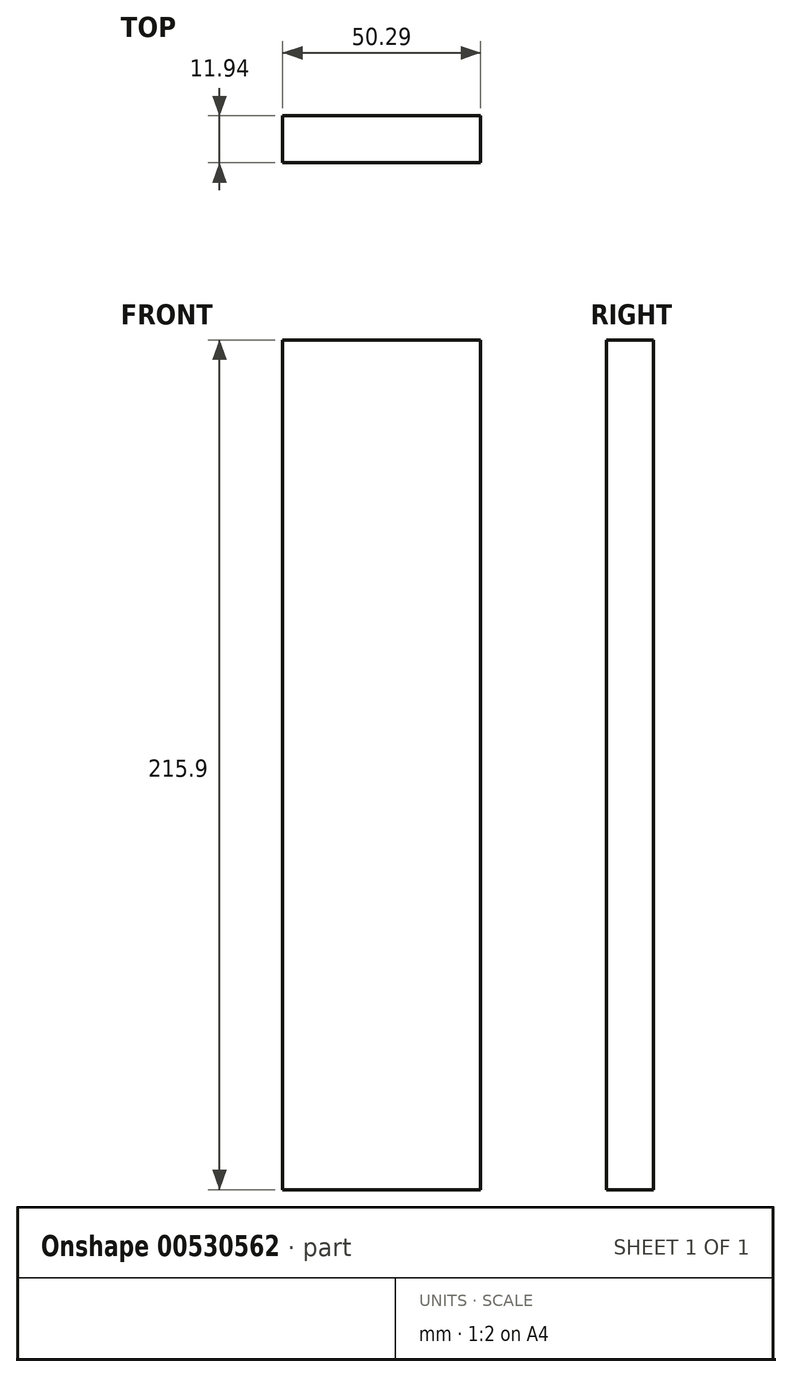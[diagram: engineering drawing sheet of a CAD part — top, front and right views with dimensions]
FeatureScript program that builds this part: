
annotation { "Feature Type Name" : "Feature", "Feature Type Description" : "" }
export const myFeature = defineFeature(function(context is Context, id is Id, definition is map)
    precondition{}
    {
        {
            var Q0;
            Q0=qCreatedBy(makeId("Front.planeOp"),FACE);
            var sketch = newSketch(context, id + "F0", { "sketchPlane" : qUnion([Q0])});
            skLineSegment(sketch, "E0.bottom", {"start": v(0, 0) * mm, "end": v(50.3, 0) * mm});
            skLineSegment(sketch, "E0.top", {"start": v(0, -215.9) * mm, "end": v(50.3, -215.9) * mm});
            skLineSegment(sketch, "E0.left", {"start": v(0, 0) * mm, "end": v(0, -215.9) * mm});
            skLineSegment(sketch, "E0.right", {"start": v(50.3, 0) * mm, "end": v(50.3, -215.9) * mm});
            skSolve(sketch);
        }
        {
            var Q0;
            Q0 = qSketchRegion(id + "F0", true);
            extrude(context, id + "F1", {"entities" : qUnion([Q0]), "depth" : 11.94 * mm, "offsetDistance" : 25.4 * mm});
        }
    });
